# Revit family: 305_A55GY005
name_source: partatom
category: Pipe Accessories
revit_build: Autodesk Revit 2018 (Build: 20170223_1515(x64)
units: mm (PartAtom-declared; Revit-internal decimal feet)

## family parameters
Always vertical = Yes
Cut with Voids When Loaded = No
Part Type = Valve - Breaks Into
Round Connector Dimension = Use Diameter
Shared = No
Work Plane-Based = No

## types (1)
- A55GY005
    A2 = 65 mm  [stored 0.213255 ft]
    BH = 91 mm
    CAT0 = Yes
    CenSd_RN_6 = 39 mm
    D = 65 mm
    Description = GROOVE ANGLE HOSE VALVE
    HB = 127 mm
    HH = 25 mm  [stored 0.082021 ft]
    HH__ve = -25 mm  [stored -0.082021 ft]
    HN = 19 mm
    HP = 30 mm  [stored 0.0984252 ft]
    HP__ve = -30 mm
    HT = 194 mm
    L = 80 mm
    L2D = 80 mm
    L2D_Min = 3048 mm  [stored 10 ft]
    MC_Default_elevation = 0 mm  [stored 0 ft]
    Manufacturer = Giacomini
    QmdConnectorList = 301;D;302;D
    R1 = 20 mm  [stored 0.0656168 ft]
    R12 = 10 mm  [stored 0.0328084 ft]
    RB = 56 mm
    RN = 45 mm
    RP = 42 mm
    TH = 84 mm
    URL = http://www.giacomini.com
    W2D = 65 mm  [stored 0.213255 ft]
    magiPartTypeId = 305
    magiProductCode = A55GY005
    magiProductFamilyId = A55GY005
    magiProductId = A55GY005

note: [stored X ft] marks values corroborated as IEEE doubles in the binary element streams (Revit-internal decimal feet)

## geometry (parser evidence)
native form markers: Sweep x3
no freeform markers — native parametric forms only
